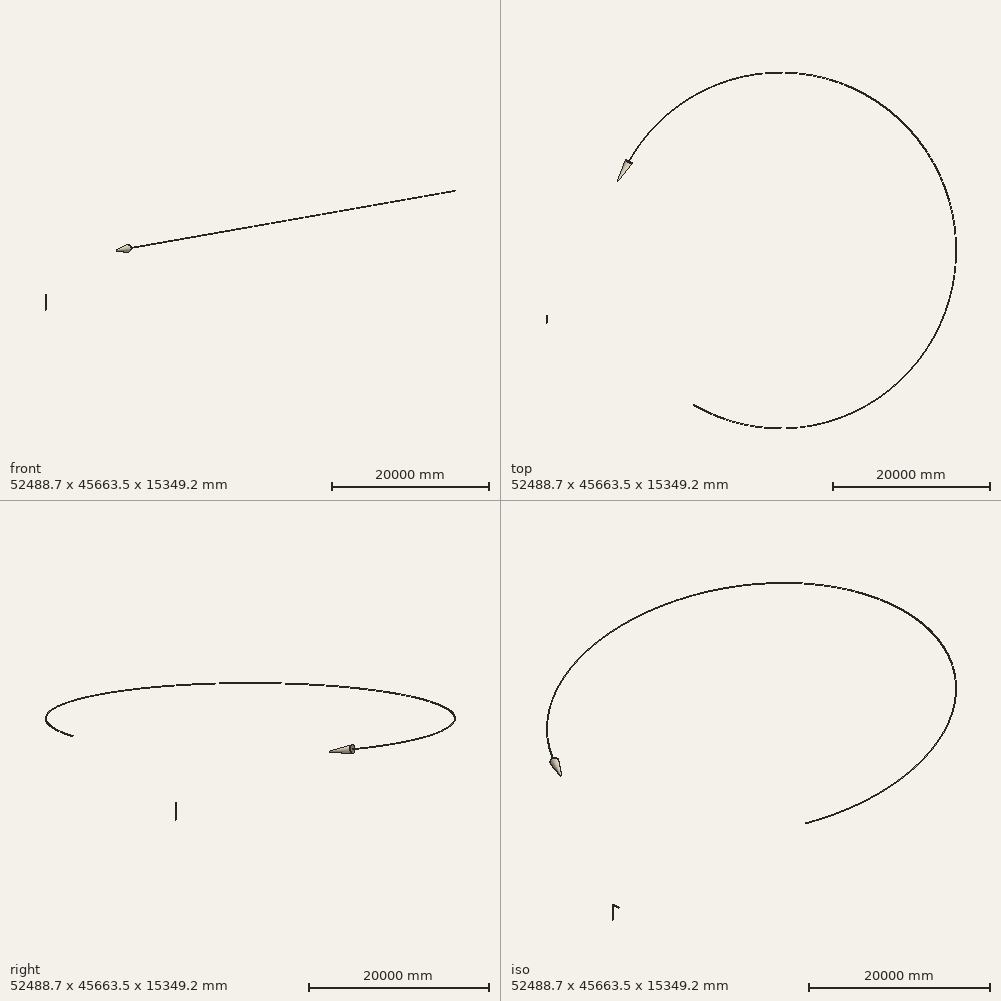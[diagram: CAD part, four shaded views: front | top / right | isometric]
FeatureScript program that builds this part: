
annotation { "Feature Type Name" : "Feature", "Feature Type Description" : "" }
export const myFeature = defineFeature(function(context is Context, id is Id, definition is map)
    precondition{}
    {
        {
            var Q0;
            Q0=qCreatedBy(makeId("Top.planeOp"),FACE);
            var sketch = newSketch(context, id + "F0", { "sketchPlane" : qUnion([Q0])});
            skArc(sketch, "E0", {"start": v(22781.75, 0) * mm, "mid": v(38890.87, 38890.87) * mm, "end": v(0, 22781.75) * mm});
            skSolve(sketch);
        }
        {
            var Q0;
            Q0=sQuery(id+"F0.wireOp",EDGE,"E0");
            var Q1;
            Q1=sQuery(id+"F0.wireOp",VERTEX,"E0.start");
            cPlane(context, id + "F1", {"entities" : qUnion([Q0, Q1]), "cplaneType" : CPlaneType.CURVE_POINT, "offset" : 25 * mm, "width" : 150 * mm, "height" : 150 * mm});
        }
        {
            var Q0;
            Q0=qCreatedBy(id+"F1.planeOp",FACE);
            var sketch = newSketch(context, id + "F2", { "sketchPlane" : qUnion([Q0])});
            skCircle(sketch, "E1", {"center": v(0, 0) * mm, "radius": 50 * mm});
            skSolve(sketch);
        }
        {
            var Q0;
            Q0=qSketchRegion(id+"F2",true);
            var Q1;
            Q1=sQuery(id+"F0.wireOp",EDGE,"E0");
            sweep(context, id + "F3", {"profiles" : qUnion([Q0]), "path" : qUnion([Q1])});
        }
        {
            var Q0;
            Q0=makeQuery(id+"F3.opSweep","CAP_FACE",FACE,{"disambiguationData":[OSD([sQuery(id+"F0.wireOp",VERTEX,"E0.end"),sQuery(id+"F2.wireOp",EDGE,"E1")])],"isStart":false});
            var sketch = newSketch(context, id + "F4", { "sketchPlane" : qUnion([Q0])});
            skCircle(sketch, "E2", {"center": v(0, 0) * mm, "radius": 500 * mm});
            skSolve(sketch);
        }
        {
            var Q0;
            Q0=qSketchRegion(id+"F4",true);
            extrude(context, id + "F5", {"entities" : qUnion([Q0]), "operationType" : NewBodyOperationType.ADD, "depth" : 3000 * mm, "offsetDistance" : 25 * mm});
        }
        {
            var Q0;
            Q0=makeQuery(id+"F5.opExtrude","CAP_EDGE",EDGE,{"disambiguationData":[OSD([sQuery(id+"F4.wireOp",EDGE,"E2")])],"isStart":false});
            chamfer(context, id + "F6", {"entities" : qUnion([Q0]), "chamferType" : ChamferType.TWO_OFFSETS, "width1" : 2900 * mm, "oppositeDirection" : true, "width2" : 450 * mm, "tangentPropagation" : true});
        }
        {
            var Q0;
            Q0=qCreatedBy(makeId("Top.planeOp"),FACE);
            var sketch = newSketch(context, id + "F7", { "sketchPlane" : qUnion([Q0])});
            skCircle(sketch, "E3", {"center": v(0, 0) * mm, "radius": 50 * mm});
            skSolve(sketch);
        }
        {
            var Q0;
            Q0=qSketchRegion(id+"F7",true);
            extrude(context, id + "F8", {"entities" : qUnion([Q0]), "oppositeDirection" : true, "depth" : 2000 * mm, "offsetDistance" : 25 * mm});
        }
        {
            var Q0;
            Q0=makeQuery(id+"F3.opSweep","SWEPT_BODY",BODY,{"disambiguationData":[OSD([sQuery(id+"F0.wireOp",EDGE,"E0"),sQuery(id+"F2.wireOp",EDGE,"E1")])]});
            var Q1;
            Q1=makeQuery(id+"F8.opExtrude","SWEPT_FACE",FACE,{"disambiguationData":[OSD([sQuery(id+"F7.wireOp",EDGE,"E3")])]});
            transform(context, id + "F9", {"entities" : qUnion([Q0]), "transformType" : TransformType.ROTATION, "transformAxis" : qUnion([Q1]), "angle" : 30 * degree, "oppositeDirection" : true, "makeCopy" : false});
        }
        {
            var Q0;
            Q0=makeQuery(id+"F3.opSweep","SWEPT_BODY",BODY,{"disambiguationData":[OSD([sQuery(id+"F0.wireOp",EDGE,"E0"),sQuery(id+"F2.wireOp",EDGE,"E1")])]});
            transform(context, id + "F10", {"entities" : qUnion([Q0]), "transformType" : TransformType.TRANSLATION_3D, "dx" : 0 * mm, "dy" : 0 * mm, "dz" : 4000 * mm, "makeCopy" : false});
        }
        {
            var Q0;
            Q0=qCreatedBy(makeId("Front.planeOp"),FACE);
            var sketch = newSketch(context, id + "F11", { "sketchPlane" : qUnion([Q0])});
            skCircle(sketch, "E4", {"center": v(0, 0) * mm, "radius": 50 * mm});
            skSolve(sketch);
        }
        {
            var Q0;
            Q0=qSketchRegion(id+"F11",true);
            extrude(context, id + "F12", {"entities" : qUnion([Q0]), "operationType" : NewBodyOperationType.ADD, "depth" : 1000 * mm, "offsetDistance" : 25 * mm});
        }
        {
            var Q0;
            Q0=makeQuery(id+"F3.opSweep","SWEPT_BODY",BODY,{"disambiguationData":[OSD([sQuery(id+"F0.wireOp",EDGE,"E0"),sQuery(id+"F2.wireOp",EDGE,"E1")])]});
            var Q1;
            Q1=makeQuery(id+"F12.opExtrude","SWEPT_FACE",FACE,{"disambiguationData":[OSD([sQuery(id+"F11.wireOp",EDGE,"E4")])]});
            transform(context, id + "F13", {"entities" : qUnion([Q0]), "transformType" : TransformType.ROTATION, "transformAxis" : qUnion([Q1]), "angle" : 10 * degree, "oppositeDirection" : true, "makeCopy" : false});
        }
    });
